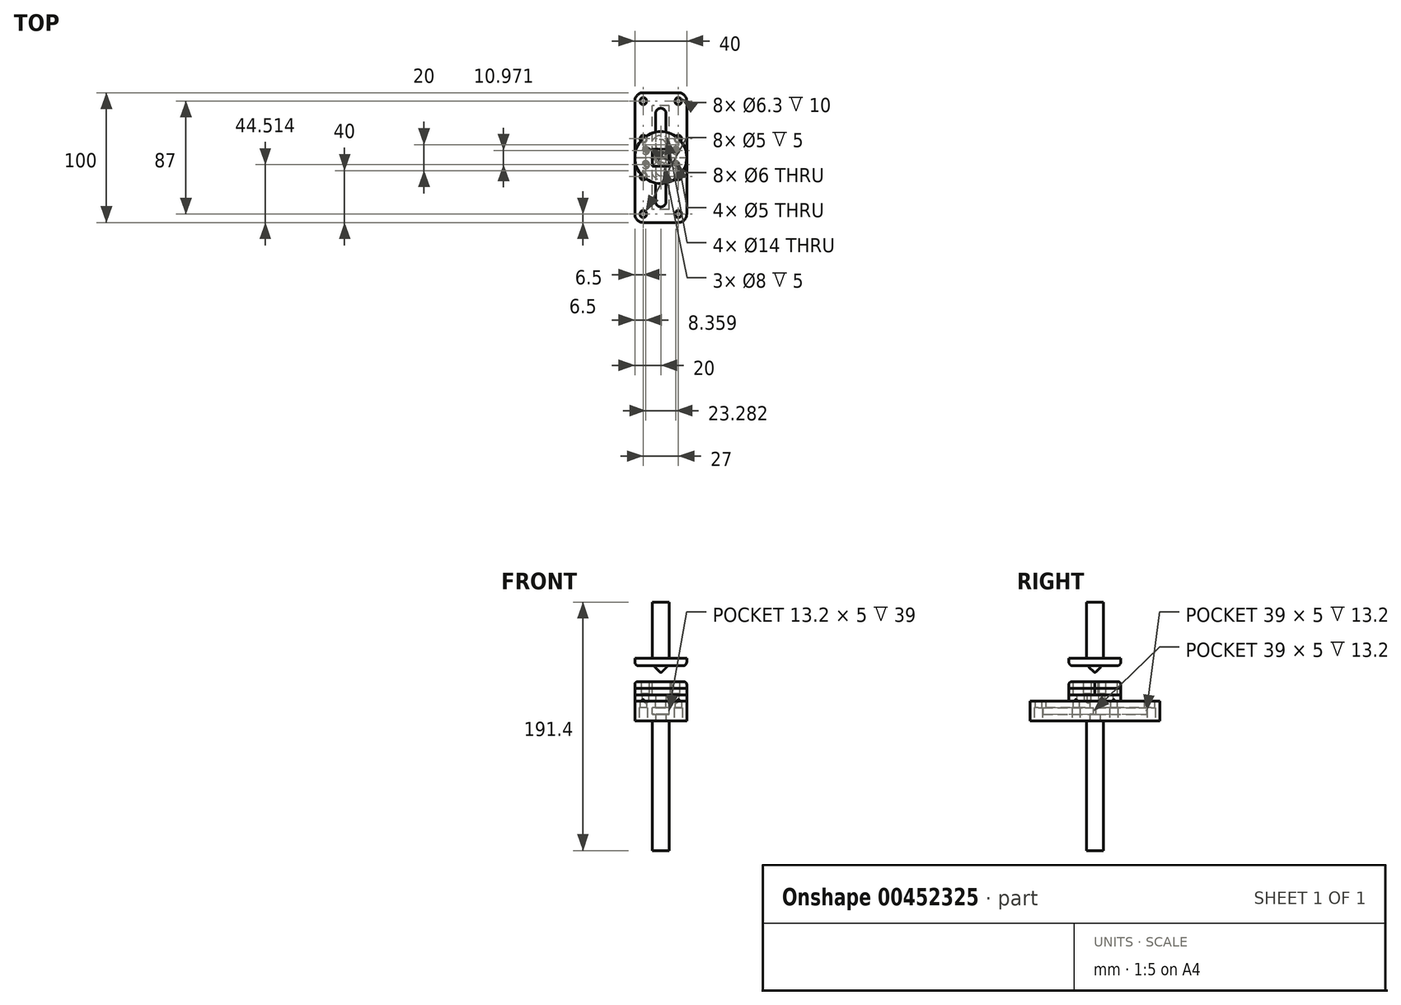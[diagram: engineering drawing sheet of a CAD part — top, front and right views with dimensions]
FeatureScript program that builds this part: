
annotation { "Feature Type Name" : "Feature", "Feature Type Description" : "" }
export const myFeature = defineFeature(function(context is Context, id is Id, definition is map)
    precondition{}
    {
        {
            var Q0;
            Q0=qCreatedBy(makeId("Top.planeOp"),FACE);
            var sketch = newSketch(context, id + "F0", { "sketchPlane" : qUnion([Q0])});
            skLineSegment(sketch, "E0.bottom", {"start": v(6.5, 6.5) * mm, "end": v(-6.5, 6.5) * mm});
            skLineSegment(sketch, "E0.top", {"start": v(6.5, -6.5) * mm, "end": v(-6.5, -6.5) * mm});
            skLineSegment(sketch, "E0.left", {"start": v(6.5, 6.5) * mm, "end": v(6.5, -6.5) * mm});
            skLineSegment(sketch, "E0.right", {"start": v(-6.5, 6.5) * mm, "end": v(-6.5, -6.5) * mm});
            skPoint(sketch, "E0.middle", {"position": v(0, 0) * mm});
            skSolve(sketch);
        }
        {
            var Q0;
            Q0 = qSketchRegion(id + "F0", true);
            extrude(context, id + "F1", {"entities" : qUnion([Q0]), "oppositeDirection" : true, "depth" : 100 * mm});
        }
        {
            var Q0;
            Q0=qCreatedBy(makeId("Top.planeOp"),FACE);
            var sketch = newSketch(context, id + "F2", { "sketchPlane" : qUnion([Q0])});
            skLineSegment(sketch, "E1.bottom", {"start": v(20, 50) * mm, "end": v(-20, 50) * mm});
            skLineSegment(sketch, "E1.top", {"start": v(20, -50) * mm, "end": v(-20, -50) * mm});
            skLineSegment(sketch, "E1.left", {"start": v(20, 50) * mm, "end": v(20, -50) * mm});
            skLineSegment(sketch, "E1.right", {"start": v(-20, 50) * mm, "end": v(-20, -50) * mm});
            skPoint(sketch, "E1.middle", {"position": v(0, 0) * mm});
            skCircle(sketch, "E2", {"center": v(0, 0) * mm, "radius": 4 * mm});
            skSolve(sketch);
        }
        {
            var Q0;
            Q0 = qSketchRegion(id + "F2", true);
            extrude(context, id + "F3", {"entities" : qUnion([Q0]), "depth" : 5 * mm});
        }
        {
            var Q0;
            Q0=makeQuery(id+"F3.opExtrude","CAP_FACE",FACE,{"disambiguationData":[OSD([sQuery(id+"F2.wireOp",EDGE,"E1.bottom"),sQuery(id+"F2.wireOp",EDGE,"E1.top"),sQuery(id+"F2.wireOp",EDGE,"E1.left"),sQuery(id+"F2.wireOp",EDGE,"E1.right")])],"isStart":false});
            var sketch = newSketch(context, id + "F4", { "sketchPlane" : qUnion([Q0])});
            skLineSegment(sketch, "E3.bottom", {"start": v(-20, -50) * mm, "end": v(20, -50) * mm});
            skLineSegment(sketch, "E3.top", {"start": v(-20, 50) * mm, "end": v(20, 50) * mm});
            skLineSegment(sketch, "E3.left", {"start": v(-20, -50) * mm, "end": v(-20, 50) * mm});
            skLineSegment(sketch, "E3.right", {"start": v(20, -50) * mm, "end": v(20, 50) * mm});
            skLineSegment(sketch, "E4.bottom", {"start": v(6.6, -40) * mm, "end": v(-6.6, -40) * mm});
            skLineSegment(sketch, "E4.top", {"start": v(6.6, 40) * mm, "end": v(-6.6, 40) * mm});
            skLineSegment(sketch, "E4.left", {"start": v(6.6, -40) * mm, "end": v(6.6, 40) * mm});
            skLineSegment(sketch, "E4.right", {"start": v(-6.6, -40) * mm, "end": v(-6.6, 40) * mm});
            skPoint(sketch, "E4.middle", {"position": v(0, 0) * mm});
            skSolve(sketch);
        }
        {
            var Q0;
            Q0 = qSketchRegion(id + "F4", true);
            extrude(context, id + "F5", {"entities" : qUnion([Q0]), "depth" : 5 * mm});
        }
        {
            var Q0;
            Q0=makeQuery(id+"F5.opExtrude","CAP_FACE",FACE,{"disambiguationData":[OSD([sQuery(id+"F4.wireOp",EDGE,"E3.bottom"),sQuery(id+"F4.wireOp",EDGE,"E3.top"),sQuery(id+"F4.wireOp",EDGE,"E3.left"),sQuery(id+"F4.wireOp",EDGE,"E3.right"),sQuery(id+"F4.wireOp",EDGE,"E4.bottom"),sQuery(id+"F4.wireOp",EDGE,"E4.top"),sQuery(id+"F4.wireOp",EDGE,"E4.left"),sQuery(id+"F4.wireOp",EDGE,"E4.right")])],"isStart":false});
            var sketch = newSketch(context, id + "F6", { "sketchPlane" : qUnion([Q0])});
            skLineSegment(sketch, "E5.bottom", {"start": v(-20, -50) * mm, "end": v(20, -50) * mm});
            skLineSegment(sketch, "E5.top", {"start": v(-20, 50) * mm, "end": v(20, 50) * mm});
            skLineSegment(sketch, "E5.left", {"start": v(-20, -50) * mm, "end": v(-20, 50) * mm});
            skLineSegment(sketch, "E5.right", {"start": v(20, -50) * mm, "end": v(20, 50) * mm});
            skLineSegment(sketch, "E6.bottom", {"start": v(4, 38) * mm, "end": v(-4, 38) * mm});
            skLineSegment(sketch, "E6.top", {"start": v(4, -38) * mm, "end": v(-4, -38) * mm});
            skLineSegment(sketch, "E6.left", {"start": v(4, 38) * mm, "end": v(4, -38) * mm});
            skLineSegment(sketch, "E6.right", {"start": v(-4, 38) * mm, "end": v(-4, -38) * mm});
            skPoint(sketch, "E6.middle", {"position": v(0, 0) * mm});
            skSolve(sketch);
        }
        {
            var Q0;
            Q0 = qSketchRegion(id + "F6", true);
            extrude(context, id + "F7", {"entities" : qUnion([Q0]), "depth" : 5 * mm});
        }
        {
            var Q0;
            Q0=makeQuery(id+"F7.opExtrude","CAP_FACE",FACE,{"disambiguationData":[OSD([sQuery(id+"F6.wireOp",EDGE,"E5.bottom"),sQuery(id+"F6.wireOp",EDGE,"E5.top"),sQuery(id+"F6.wireOp",EDGE,"E5.left"),sQuery(id+"F6.wireOp",EDGE,"E5.right"),sQuery(id+"F6.wireOp",EDGE,"E6.bottom"),sQuery(id+"F6.wireOp",EDGE,"E6.top"),sQuery(id+"F6.wireOp",EDGE,"E6.left"),sQuery(id+"F6.wireOp",EDGE,"E6.right")])],"isStart":false});
            var sketch = newSketch(context, id + "F8", { "sketchPlane" : qUnion([Q0])});
            skArc(sketch, "E7", {"start": v(-20, 0) * mm, "mid": v(0, -20) * mm, "end": v(20, 0) * mm});
            skLineSegment(sketch, "E8", {"start": v(-20, 0) * mm, "end": v(20, 0) * mm});
            skCircle(sketch, "E9", {"center": v(0, -10) * mm, "radius": 4 * mm});
            skSolve(sketch);
        }
        {
            var Q0;
            Q0 = qSketchRegion(id + "F8", true);
            extrude(context, id + "F9", {"entities" : qUnion([Q0]), "depth" : 5 * mm});
        }
        {
            var Q0;
            Q0=makeQuery(id+"F9.opExtrude","SWEPT_BODY",BODY,{"disambiguationData":[OSD([sQuery(id+"F8.wireOp",EDGE,"E7"),sQuery(id+"F8.wireOp",EDGE,"E8"),sQuery(id+"F8.wireOp",EDGE,"E9")])]});
            var Q1;
            Q1=qCreatedBy(makeId("Front.planeOp"),FACE);
            mirror(context, id + "F10", {"entities" : qUnion([Q0]), "mirrorPlane" : qUnion([Q1])});
        }
        {
            var Q0;
            Q0=makeQuery(id+"F9.opExtrude","CAP_FACE",FACE,{"disambiguationData":[OSD([sQuery(id+"F8.wireOp",EDGE,"E7"),sQuery(id+"F8.wireOp",EDGE,"E8"),sQuery(id+"F8.wireOp",EDGE,"E9")])],"isStart":false});
            var sketch = newSketch(context, id + "F11", { "sketchPlane" : qUnion([Q0])});
            skArc(sketch, "E10", {"start": v(-20, 0) * mm, "mid": v(0, -20) * mm, "end": v(20, 0) * mm});
            skLineSegment(sketch, "E11", {"start": v(-20, 0) * mm, "end": v(20, 0) * mm});
            skCircle(sketch, "E12", {"center": v(0, -10) * mm, "radius": 7 * mm});
            skSolve(sketch);
        }
        {
            var Q0;
            Q0 = qSketchRegion(id + "F11", true);
            extrude(context, id + "F12", {"entities" : qUnion([Q0]), "depth" : 5 * mm});
        }
        {
            var Q0;
            Q0=makeQuery(id+"F12.opExtrude","SWEPT_BODY",BODY,{"disambiguationData":[OSD([sQuery(id+"F11.wireOp",EDGE,"E10"),sQuery(id+"F11.wireOp",EDGE,"E11"),sQuery(id+"F11.wireOp",EDGE,"E12")])]});
            var Q1;
            Q1=qCreatedBy(makeId("Front.planeOp"),FACE);
            mirror(context, id + "F13", {"entities" : qUnion([Q0]), "mirrorPlane" : qUnion([Q1])});
        }
        {
            var Q0;
            Q0=makeQuery(id+"F3.opExtrude","SWEPT_EDGE",EDGE,{"disambiguationData":[OSD([sQuery(id+"F2.wireOp",EDGE,"E1.top"),sQuery(id+"F2.wireOp",EDGE,"E1.left")])]});
            var Q1;
            Q1=makeQuery(id+"F5.opExtrude","SWEPT_EDGE",EDGE,{"disambiguationData":[OSD([sQuery(id+"F4.wireOp",EDGE,"E3.bottom"),sQuery(id+"F4.wireOp",EDGE,"E3.right")])]});
            var Q2;
            Q2=makeQuery(id+"F7.opExtrude","SWEPT_EDGE",EDGE,{"disambiguationData":[OSD([sQuery(id+"F6.wireOp",EDGE,"E5.bottom"),sQuery(id+"F6.wireOp",EDGE,"E5.right")])]});
            var Q3;
            Q3=makeQuery(id+"F3.opExtrude","SWEPT_EDGE",EDGE,{"disambiguationData":[OSD([sQuery(id+"F2.wireOp",EDGE,"E1.top"),sQuery(id+"F2.wireOp",EDGE,"E1.right")])]});
            var Q4;
            Q4=makeQuery(id+"F5.opExtrude","SWEPT_EDGE",EDGE,{"disambiguationData":[OSD([sQuery(id+"F4.wireOp",EDGE,"E3.bottom"),sQuery(id+"F4.wireOp",EDGE,"E3.left")])]});
            var Q5;
            Q5=makeQuery(id+"F7.opExtrude","SWEPT_EDGE",EDGE,{"disambiguationData":[OSD([sQuery(id+"F6.wireOp",EDGE,"E5.bottom"),sQuery(id+"F6.wireOp",EDGE,"E5.left")])]});
            var Q6;
            Q6=makeQuery(id+"F3.opExtrude","SWEPT_EDGE",EDGE,{"disambiguationData":[OSD([sQuery(id+"F2.wireOp",EDGE,"E1.bottom"),sQuery(id+"F2.wireOp",EDGE,"E1.right")])]});
            var Q7;
            Q7=makeQuery(id+"F5.opExtrude","SWEPT_EDGE",EDGE,{"disambiguationData":[OSD([sQuery(id+"F4.wireOp",EDGE,"E3.top"),sQuery(id+"F4.wireOp",EDGE,"E3.left")])]});
            var Q8;
            Q8=makeQuery(id+"F7.opExtrude","SWEPT_EDGE",EDGE,{"disambiguationData":[OSD([sQuery(id+"F6.wireOp",EDGE,"E5.top"),sQuery(id+"F6.wireOp",EDGE,"E5.left")])]});
            var Q9;
            Q9=makeQuery(id+"F7.opExtrude","SWEPT_EDGE",EDGE,{"disambiguationData":[OSD([sQuery(id+"F6.wireOp",EDGE,"E5.top"),sQuery(id+"F6.wireOp",EDGE,"E5.right")])]});
            var Q10;
            Q10=makeQuery(id+"F5.opExtrude","SWEPT_EDGE",EDGE,{"disambiguationData":[OSD([sQuery(id+"F4.wireOp",EDGE,"E3.top"),sQuery(id+"F4.wireOp",EDGE,"E3.right")])]});
            var Q11;
            Q11=makeQuery(id+"F3.opExtrude","SWEPT_EDGE",EDGE,{"disambiguationData":[OSD([sQuery(id+"F2.wireOp",EDGE,"E1.bottom"),sQuery(id+"F2.wireOp",EDGE,"E1.left")])]});
            fillet(context, id + "F14", {"entities" : qUnion([Q0, Q1, Q2, Q3, Q4, Q5, Q6, Q7, Q8, Q9, Q10, Q11]), "radius" : 6.5 * mm, "tangentPropagation" : true, "allowEdgeOverflow" : false});
        }
        {
            var Q0;
            Q0=makeQuery(id+"F7.opExtrude","SWEPT_EDGE",EDGE,{"disambiguationData":[OSD([sQuery(id+"F6.wireOp",EDGE,"E6.bottom"),sQuery(id+"F6.wireOp",EDGE,"E6.left")])]});
            var Q1;
            Q1=makeQuery(id+"F7.opExtrude","SWEPT_EDGE",EDGE,{"disambiguationData":[OSD([sQuery(id+"F6.wireOp",EDGE,"E6.bottom"),sQuery(id+"F6.wireOp",EDGE,"E6.right")])]});
            var Q2;
            Q2=makeQuery(id+"F7.opExtrude","SWEPT_EDGE",EDGE,{"disambiguationData":[OSD([sQuery(id+"F6.wireOp",EDGE,"E6.top"),sQuery(id+"F6.wireOp",EDGE,"E6.right")])]});
            var Q3;
            Q3=makeQuery(id+"F7.opExtrude","SWEPT_EDGE",EDGE,{"disambiguationData":[OSD([sQuery(id+"F6.wireOp",EDGE,"E6.top"),sQuery(id+"F6.wireOp",EDGE,"E6.left")])]});
            fillet(context, id + "F15", {"entities" : qUnion([Q0, Q1, Q2, Q3]), "radius" : 4 * mm, "tangentPropagation" : true, "allowEdgeOverflow" : false});
        }
        {
            var Q0;
            Q0=makeQuery(id+"F3.opExtrude","CAP_FACE",FACE,{"disambiguationData":[OSD([sQuery(id+"F2.wireOp",EDGE,"E1.bottom"),sQuery(id+"F2.wireOp",EDGE,"E1.top"),sQuery(id+"F2.wireOp",EDGE,"E1.left"),sQuery(id+"F2.wireOp",EDGE,"E1.right")])],"isStart":true});
            var sketch = newSketch(context, id + "F16", { "sketchPlane" : qUnion([Q0])});
            skCircle(sketch, "E13", {"center": v(13.5, 43.5) * mm, "radius": 3 * mm});
            skCircle(sketch, "E14.0.1.0", {"center": v(13.5, 14.5) * mm, "radius": 3 * mm});
            skCircle(sketch, "E14.0.2.0", {"center": v(13.5, -14.5) * mm, "radius": 3 * mm});
            skCircle(sketch, "E14.0.3.0", {"center": v(13.5, -43.5) * mm, "radius": 3 * mm});
            skCircle(sketch, "E14.1.0.0", {"center": v(-13.5, 43.5) * mm, "radius": 3 * mm});
            skCircle(sketch, "E14.1.1.0", {"center": v(-13.5, 14.5) * mm, "radius": 3 * mm});
            skCircle(sketch, "E14.1.2.0", {"center": v(-13.5, -14.5) * mm, "radius": 3 * mm});
            skCircle(sketch, "E14.1.3.0", {"center": v(-13.5, -43.5) * mm, "radius": 3 * mm});
            skLineSegment(sketch, "E14.direction1", {"start": v(13.5, 43.5) * mm, "end": v(-13.5, 43.5) * mm, "construction": true});
            skLineSegment(sketch, "E14.direction2", {"start": v(13.5, 43.5) * mm, "end": v(13.5, 14.5) * mm, "construction": true});
            skSolve(sketch);
        }
        {
            var Q0;
            Q0=sQuery(id+"F16.wireOp",VERTEX,"E14.direction1.end");
            var Q1;
            Q1=sQuery(id+"F16.wireOp",VERTEX,"E14.1.1.0.center");
            var Q2;
            Q2=sQuery(id+"F16.wireOp",VERTEX,"E14.0.1.0.center");
            var Q3;
            Q3=sQuery(id+"F16.wireOp",VERTEX,"E13.center");
            var Q4;
            Q4=sQuery(id+"F16.wireOp",VERTEX,"E14.0.2.0.center");
            var Q5;
            Q5=sQuery(id+"F16.wireOp",VERTEX,"E14.1.2.0.center");
            var Q6;
            Q6=sQuery(id+"F16.wireOp",VERTEX,"E14.1.3.0.center");
            var Q7;
            Q7=sQuery(id+"F16.wireOp",VERTEX,"E14.0.3.0.center");
            var Q8;
            Q8=makeQuery(id+"F9.opExtrude","SWEPT_BODY",BODY,{"disambiguationData":[OSD([sQuery(id+"F8.wireOp",EDGE,"E7"),sQuery(id+"F8.wireOp",EDGE,"E8"),sQuery(id+"F8.wireOp",EDGE,"E9")])]});
            var Q9;
            Q9=makeQuery(id+"F12.opExtrude","SWEPT_BODY",BODY,{"disambiguationData":[OSD([sQuery(id+"F11.wireOp",EDGE,"E10"),sQuery(id+"F11.wireOp",EDGE,"E11"),sQuery(id+"F11.wireOp",EDGE,"E12")])]});
            var Q10;
            Q10=makeQuery(id+"F3.opExtrude","SWEPT_BODY",BODY,{"disambiguationData":[OSD([sQuery(id+"F2.wireOp",EDGE,"E1.bottom"),sQuery(id+"F2.wireOp",EDGE,"E1.top"),sQuery(id+"F2.wireOp",EDGE,"E1.left"),sQuery(id+"F2.wireOp",EDGE,"E1.right")])]});
            var Q11;
            Q11=makeQuery(id+"F5.opExtrude","SWEPT_BODY",BODY,{"disambiguationData":[OSD([sQuery(id+"F4.wireOp",EDGE,"E3.bottom"),sQuery(id+"F4.wireOp",EDGE,"E3.top"),sQuery(id+"F4.wireOp",EDGE,"E3.left"),sQuery(id+"F4.wireOp",EDGE,"E3.right"),sQuery(id+"F4.wireOp",EDGE,"E4.bottom"),sQuery(id+"F4.wireOp",EDGE,"E4.top"),sQuery(id+"F4.wireOp",EDGE,"E4.left"),sQuery(id+"F4.wireOp",EDGE,"E4.right")])]});
            var Q12;
            Q12=makeQuery(id+"F7.opExtrude","SWEPT_BODY",BODY,{"disambiguationData":[OSD([sQuery(id+"F6.wireOp",EDGE,"E5.bottom"),sQuery(id+"F6.wireOp",EDGE,"E5.top"),sQuery(id+"F6.wireOp",EDGE,"E5.left"),sQuery(id+"F6.wireOp",EDGE,"E5.right"),sQuery(id+"F6.wireOp",EDGE,"E6.bottom"),sQuery(id+"F6.wireOp",EDGE,"E6.top"),sQuery(id+"F6.wireOp",EDGE,"E6.left"),sQuery(id+"F6.wireOp",EDGE,"E6.right")])]});
            var Q13;
            Q13=makeQuery(id+"F10.opPattern","COPY",BODY,{"derivedFrom":makeQuery(id+"F9.opExtrude","SWEPT_BODY",BODY,{"disambiguationData":[OSD([sQuery(id+"F8.wireOp",EDGE,"E7"),sQuery(id+"F8.wireOp",EDGE,"E8"),sQuery(id+"F8.wireOp",EDGE,"E9")])]}),"instanceName":"1"});
            var Q14;
            Q14=makeQuery(id+"F13.opPattern","COPY",BODY,{"derivedFrom":makeQuery(id+"F12.opExtrude","SWEPT_BODY",BODY,{"disambiguationData":[OSD([sQuery(id+"F11.wireOp",EDGE,"E10"),sQuery(id+"F11.wireOp",EDGE,"E11"),sQuery(id+"F11.wireOp",EDGE,"E12")])]}),"instanceName":"1"});
            hole(context, id + "F17", {"style" : HoleStyle.SIMPLE, "endStyle" : HoleEndStyle.BLIND_IN_LAST, "standardTappedOrClearance" : lookupTablePath({ "fit" : "Close", "standard" : "ISO", "engagement" : "75%", "pitch" : "1 mm", "size" : "M6", "type" : "Clearance & tapped" }), "standardBlindInLast" : lookupTablePath({ "standard" : "ISO", "fit" : "Close", "engagement" : "75%", "pitch" : "1 mm", "size" : "M6", "type" : "Clearance & tapped" }), "holeDiameter" : 6.3 * mm, "tapDrillDiameter" : 5 * mm, "showTappedDepth" : true, "holeDepth" : 5 * mm, "isTappedThrough" : true, "tappedDepth" : 5 * mm, "tapClearance" : 0, "locations" : qUnion([Q0, Q1, Q2, Q3, Q4, Q5, Q6, Q7]), "scope" : qUnion([Q8, Q9, Q10, Q11, Q12, Q13, Q14]), "majorDiameter" : 6 * mm});
        }
        {
            var Q0;
            Q0=makeQuery(id+"F12.opExtrude","CAP_FACE",FACE,{"disambiguationData":[OSD([sQuery(id+"F11.wireOp",EDGE,"E10"),sQuery(id+"F11.wireOp",EDGE,"E11"),sQuery(id+"F11.wireOp",EDGE,"E12")])],"isStart":false});
            var sketch = newSketch(context, id + "F18", { "sketchPlane" : qUnion([Q0])});
            skArc(sketch, "E15", {"start": v(-20, 0) * mm, "mid": v(0, -20) * mm, "end": v(20, 0) * mm});
            skLineSegment(sketch, "E16", {"start": v(-20, 0) * mm, "end": v(20, 0) * mm});
            skCircle(sketch, "E17", {"center": v(0, -10) * mm, "radius": 7 * mm});
            skSolve(sketch);
        }
        {
            var Q0;
            Q0 = qSketchRegion(id + "F18", true);
            extrude(context, id + "F19", {"entities" : qUnion([Q0]), "depth" : 5 * mm});
        }
        {
            var Q0;
            Q0=makeQuery(id+"F19.opExtrude","SWEPT_BODY",BODY,{"disambiguationData":[OSD([sQuery(id+"F18.wireOp",EDGE,"E15"),sQuery(id+"F18.wireOp",EDGE,"E16"),sQuery(id+"F18.wireOp",EDGE,"E17")])]});
            var Q1;
            Q1=qCreatedBy(makeId("Front.planeOp"),FACE);
            mirror(context, id + "F20", {"entities" : qUnion([Q0]), "mirrorPlane" : qUnion([Q1])});
        }
        {
            var Q0;
            Q0=makeQuery(id+"F19.opExtrude","CAP_FACE",FACE,{"disambiguationData":[OSD([sQuery(id+"F18.wireOp",EDGE,"E15"),sQuery(id+"F18.wireOp",EDGE,"E16"),sQuery(id+"F18.wireOp",EDGE,"E17")])],"isStart":false});
            var sketch = newSketch(context, id + "F21", { "sketchPlane" : qUnion([Q0])});
            skCircle(sketch, "E18", {"center": v(11.64, -5.49) * mm, "radius": 2.99 * mm});
            skCircle(sketch, "E19.MirrorC", {"center": v(-11.64, -5.49) * mm, "radius": 2.99 * mm});
            skCircle(sketch, "E20.MirrorC", {"center": v(11.64, 5.49) * mm, "radius": 2.99 * mm});
            skCircle(sketch, "E21.MirrorC", {"center": v(-11.64, 5.49) * mm, "radius": 2.99 * mm});
            skSolve(sketch);
        }
        {
            var Q0;
            Q0=sQuery(id+"F21.wireOp",VERTEX,"E18.center");
            var Q1;
            Q1=sQuery(id+"F21.wireOp",VERTEX,"E19.MirrorC.center");
            var Q2;
            Q2=sQuery(id+"F21.wireOp",VERTEX,"E20.MirrorC.center");
            var Q3;
            Q3=sQuery(id+"F21.wireOp",VERTEX,"E21.MirrorC.center");
            var Q4;
            Q4=makeQuery(id+"F9.opExtrude","SWEPT_BODY",BODY,{"disambiguationData":[OSD([sQuery(id+"F8.wireOp",EDGE,"E7"),sQuery(id+"F8.wireOp",EDGE,"E8"),sQuery(id+"F8.wireOp",EDGE,"E9")])]});
            var Q5;
            Q5=makeQuery(id+"F12.opExtrude","SWEPT_BODY",BODY,{"disambiguationData":[OSD([sQuery(id+"F11.wireOp",EDGE,"E10"),sQuery(id+"F11.wireOp",EDGE,"E11"),sQuery(id+"F11.wireOp",EDGE,"E12")])]});
            var Q6;
            Q6=makeQuery(id+"F10.opPattern","COPY",BODY,{"derivedFrom":makeQuery(id+"F9.opExtrude","SWEPT_BODY",BODY,{"disambiguationData":[OSD([sQuery(id+"F8.wireOp",EDGE,"E7"),sQuery(id+"F8.wireOp",EDGE,"E8"),sQuery(id+"F8.wireOp",EDGE,"E9")])]}),"instanceName":"1"});
            var Q7;
            Q7=makeQuery(id+"F13.opPattern","COPY",BODY,{"derivedFrom":makeQuery(id+"F12.opExtrude","SWEPT_BODY",BODY,{"disambiguationData":[OSD([sQuery(id+"F11.wireOp",EDGE,"E10"),sQuery(id+"F11.wireOp",EDGE,"E11"),sQuery(id+"F11.wireOp",EDGE,"E12")])]}),"instanceName":"1"});
            var Q8;
            Q8=makeQuery(id+"F19.opExtrude","SWEPT_BODY",BODY,{"disambiguationData":[OSD([sQuery(id+"F18.wireOp",EDGE,"E15"),sQuery(id+"F18.wireOp",EDGE,"E16"),sQuery(id+"F18.wireOp",EDGE,"E17")])]});
            var Q9;
            Q9=makeQuery(id+"F20.opPattern","COPY",BODY,{"derivedFrom":makeQuery(id+"F19.opExtrude","SWEPT_BODY",BODY,{"disambiguationData":[OSD([sQuery(id+"F18.wireOp",EDGE,"E15"),sQuery(id+"F18.wireOp",EDGE,"E16"),sQuery(id+"F18.wireOp",EDGE,"E17")])]}),"instanceName":"1"});
            hole(context, id + "F22", {"style" : HoleStyle.SIMPLE, "endStyle" : HoleEndStyle.BLIND, "holeDiameter" : 6 * mm, "holeDepth" : 9 * mm, "isTappedThrough" : true, "tappedDepth" : 5 * mm, "tapClearance" : 0, "locations" : qUnion([Q0, Q1, Q2, Q3]), "scope" : qUnion([Q4, Q5, Q6, Q7, Q8, Q9])});
        }
        {
            var Q0;
            Q0=sQuery(id+"F21.wireOp",VERTEX,"E19.MirrorC.center");
            var Q1;
            Q1=sQuery(id+"F21.wireOp",VERTEX,"E20.MirrorC.center");
            var Q2;
            Q2=sQuery(id+"F21.wireOp",VERTEX,"E21.MirrorC.center");
            var Q3;
            Q3=sQuery(id+"F21.wireOp",VERTEX,"E20.MirrorC.center");
            var Q4;
            Q4=sQuery(id+"F21.wireOp",VERTEX,"E18.center");
            var Q5;
            Q5=makeQuery(id+"F9.opExtrude","SWEPT_BODY",BODY,{"disambiguationData":[OSD([sQuery(id+"F8.wireOp",EDGE,"E7"),sQuery(id+"F8.wireOp",EDGE,"E8"),sQuery(id+"F8.wireOp",EDGE,"E9")])]});
            var Q6;
            Q6=makeQuery(id+"F7.opExtrude","SWEPT_BODY",BODY,{"disambiguationData":[OSD([sQuery(id+"F6.wireOp",EDGE,"E5.bottom"),sQuery(id+"F6.wireOp",EDGE,"E5.top"),sQuery(id+"F6.wireOp",EDGE,"E5.left"),sQuery(id+"F6.wireOp",EDGE,"E5.right"),sQuery(id+"F6.wireOp",EDGE,"E6.bottom"),sQuery(id+"F6.wireOp",EDGE,"E6.top"),sQuery(id+"F6.wireOp",EDGE,"E6.left"),sQuery(id+"F6.wireOp",EDGE,"E6.right")])]});
            var Q7;
            Q7=makeQuery(id+"F10.opPattern","COPY",BODY,{"derivedFrom":makeQuery(id+"F9.opExtrude","SWEPT_BODY",BODY,{"disambiguationData":[OSD([sQuery(id+"F8.wireOp",EDGE,"E7"),sQuery(id+"F8.wireOp",EDGE,"E8"),sQuery(id+"F8.wireOp",EDGE,"E9")])]}),"instanceName":"1"});
            hole(context, id + "F23", {"style" : HoleStyle.SIMPLE, "endStyle" : HoleEndStyle.BLIND, "holeDiameter" : 5 * mm, "holeDepth" : 5 * mm, "isTappedThrough" : true, "tappedDepth" : 5 * mm, "tapClearance" : 0, "locations" : qUnion([Q0, Q1, Q2, Q3, Q4]), "scope" : qUnion([Q5, Q6, Q7])});
        }
        {
            var Q0;
            Q0=makeQuery(id+"F20.opPattern","COPY",EDGE,{"derivedFrom":makeQuery(id+"F19.opExtrude","CAP_EDGE",EDGE,{"disambiguationData":[OSD([sQuery(id+"F18.wireOp",EDGE,"E15")])],"isStart":false}),"instanceName":"1"});
            var Q1;
            Q1=makeQuery(id+"F19.opExtrude","CAP_EDGE",EDGE,{"disambiguationData":[OSD([sQuery(id+"F18.wireOp",EDGE,"E15")])],"isStart":false});
            fillet(context, id + "F24", {"entities" : qUnion([Q0, Q1]), "radius" : 2 * mm, "tangentPropagation" : true, "allowEdgeOverflow" : false});
        }
        {
            var Q0;
            Q0=makeQuery(id+"F21.imprint","IMPRINT",FACE,{"disambiguationData":[TD([[makeQuery(id+"F21.imprint","IMPRINT",EDGE,{"derivedFrom":sQuery(id+"F21.wireOp",EDGE,"E18")}),-1.0]])]});
            var sketch = newSketch(context, id + "F25", { "sketchPlane" : qUnion([Q0])});
            skLineSegment(sketch, "E22.bottom", {"start": v(-6.5, -6.5) * mm, "end": v(6.5, -6.5) * mm});
            skLineSegment(sketch, "E22.top", {"start": v(-6.5, 6.5) * mm, "end": v(6.5, 6.5) * mm});
            skLineSegment(sketch, "E22.left", {"start": v(-6.5, -6.5) * mm, "end": v(-6.5, 6.5) * mm});
            skLineSegment(sketch, "E22.right", {"start": v(6.5, -6.5) * mm, "end": v(6.5, 6.5) * mm});
            skPoint(sketch, "E22.middle", {"position": v(0, 0) * mm});
            skSolve(sketch);
        }
        {
            var Q0;
            Q0 = qSketchRegion(id + "F25", true);
            extrude(context, id + "F26", {"entities" : qUnion([Q0]), "depth" : 61.4 * mm, "hasSecondDirection" : true, "secondDirectionOppositeDirection" : false, "secondDirectionDepth" : 18.3 * mm});
        }
        {
            var Q0;
            Q0=makeQuery(id+"F26.opExtrude","CAP_FACE",FACE,{"disambiguationData":[OSD([sQuery(id+"F25.wireOp",EDGE,"E22.bottom"),sQuery(id+"F25.wireOp",EDGE,"E22.top"),sQuery(id+"F25.wireOp",EDGE,"E22.left"),sQuery(id+"F25.wireOp",EDGE,"E22.right")])],"isStart":true});
            var sketch = newSketch(context, id + "F27", { "sketchPlane" : qUnion([Q0])});
            skCircle(sketch, "E23", {"center": v(0, 0) * mm, "radius": 20 * mm});
            skSolve(sketch);
        }
        {
            var Q0;
            Q0 = qSketchRegion(id + "F27", true);
            extrude(context, id + "F28", {"entities" : qUnion([Q0]), "operationType" : NewBodyOperationType.ADD, "depth" : 6 * mm});
        }
        {
            var Q0;
            Q0=makeQuery(id+"F28.opExtrude","CAP_EDGE",EDGE,{"disambiguationData":[OSD([sQuery(id+"F27.wireOp",EDGE,"E23")])],"isStart":false});
            fillet(context, id + "F29", {"entities" : qUnion([Q0]), "radius" : 3 * mm, "tangentPropagation" : true, "allowEdgeOverflow" : false});
        }
        {
            var Q0;
            Q0=makeQuery(id+"F28.opExtrude","CAP_FACE",FACE,{"disambiguationData":[OSD([sQuery(id+"F27.wireOp",EDGE,"E23")])],"isStart":false});
            var sketch = newSketch(context, id + "F30", { "sketchPlane" : qUnion([Q0])});
            skCircle(sketch, "E24", {"center": v(0, 0) * mm, "radius": 5 * mm});
            skSolve(sketch);
        }
        {
            var Q0;
            Q0 = qSketchRegion(id + "F30", true);
            extrude(context, id + "F31", {"entities" : qUnion([Q0]), "depth" : 5 * mm});
        }
        {
            var Q0;
            Q0=makeQuery(id+"F31.opExtrude","CAP_EDGE",EDGE,{"disambiguationData":[OSD([sQuery(id+"F30.wireOp",EDGE,"E24")])],"isStart":false});
            chamfer(context, id + "F32", {"entities" : qUnion([Q0]), "width" : 4.5 * mm, "tangentPropagation" : true});
        }
        {
            var Q0;
            {var subQ0=sQuery(id+"F30.wireOp",EDGE,"E24");Q0=makeQuery(id+"F32.opChamfer","BLEND_EDGE",EDGE,{"blendedFrom":[makeQuery(id+"F31.opExtrude","CAP_EDGE",EDGE,{"disambiguationData":[OSD([subQ0])],"isStart":false}),makeQuery(id+"F31.opExtrude","CAP_FACE",FACE,{"disambiguationData":[OSD([subQ0])],"isStart":false})],"blendedInto":[makeQuery(id+"F31.opExtrude","CAP_FACE",FACE,{"disambiguationData":[OSD([subQ0])],"isStart":false})]});}
            fillet(context, id + "F33", {"entities" : qUnion([Q0]), "radius" : 1 * mm, "tangentPropagation" : true, "allowEdgeOverflow" : false});
        }
        {
            var Q0;
            {var subQ0=sQuery(id+"F30.wireOp",EDGE,"E24");Q0=makeQuery(id+"F32.opChamfer","BLEND_EDGE",EDGE,{"blendedFrom":[makeQuery(id+"F31.opExtrude","CAP_EDGE",EDGE,{"disambiguationData":[OSD([subQ0])],"isStart":false}),makeQuery(id+"F31.opExtrude","SWEPT_FACE",FACE,{"disambiguationData":[OSD([subQ0])]})],"blendedInto":[makeQuery(id+"F31.opExtrude","SWEPT_FACE",FACE,{"disambiguationData":[OSD([subQ0])]})]});}
            fillet(context, id + "F34", {"entities" : qUnion([Q0]), "radius" : 2 * mm, "tangentPropagation" : true, "allowEdgeOverflow" : false});
        }
        {
            var Q0;
            Q0=makeQuery(id+"F5.opExtrude","CAP_FACE",FACE,{"disambiguationData":[OSD([sQuery(id+"F4.wireOp",EDGE,"E3.bottom"),sQuery(id+"F4.wireOp",EDGE,"E3.top"),sQuery(id+"F4.wireOp",EDGE,"E3.left"),sQuery(id+"F4.wireOp",EDGE,"E3.right"),sQuery(id+"F4.wireOp",EDGE,"E4.bottom"),sQuery(id+"F4.wireOp",EDGE,"E4.top"),sQuery(id+"F4.wireOp",EDGE,"E4.left"),sQuery(id+"F4.wireOp",EDGE,"E4.right")])],"isStart":false});
            var sketch = newSketch(context, id + "F35", { "sketchPlane" : qUnion([Q0])});
            skLineSegment(sketch, "E25.bottom", {"start": v(-6.6, 1) * mm, "end": v(6.6, 1) * mm});
            skLineSegment(sketch, "E25.top", {"start": v(-6.6, -1) * mm, "end": v(6.6, -1) * mm});
            skLineSegment(sketch, "E25.left", {"start": v(-6.6, 1) * mm, "end": v(-6.6, -1) * mm});
            skLineSegment(sketch, "E25.right", {"start": v(6.6, 1) * mm, "end": v(6.6, -1) * mm});
            skPoint(sketch, "E25.middle", {"position": v(0, 0) * mm});
            skSolve(sketch);
        }
        {
            var Q0;
            Q0 = qSketchRegion(id + "F35", true);
            extrude(context, id + "F36", {"entities" : qUnion([Q0]), "operationType" : NewBodyOperationType.ADD, "oppositeDirection" : true, "depth" : 5 * mm, "offsetDistance" : 25 * mm});
        }
        {
            var Q0;
            Q0=makeQuery(id+"F7.opExtrude","CAP_FACE",FACE,{"disambiguationData":[OSD([sQuery(id+"F6.wireOp",EDGE,"E5.bottom"),sQuery(id+"F6.wireOp",EDGE,"E5.top"),sQuery(id+"F6.wireOp",EDGE,"E5.left"),sQuery(id+"F6.wireOp",EDGE,"E5.right"),sQuery(id+"F6.wireOp",EDGE,"E6.bottom"),sQuery(id+"F6.wireOp",EDGE,"E6.top"),sQuery(id+"F6.wireOp",EDGE,"E6.left"),sQuery(id+"F6.wireOp",EDGE,"E6.right")])],"isStart":false});
            var sketch = newSketch(context, id + "F37", { "sketchPlane" : qUnion([Q0])});
            skLineSegment(sketch, "E26.bottom", {"start": v(-4, -3.5) * mm, "end": v(4, -3.5) * mm});
            skLineSegment(sketch, "E26.top", {"start": v(-4, 3.5) * mm, "end": v(4, 3.5) * mm});
            skLineSegment(sketch, "E26.left", {"start": v(-4, -3.5) * mm, "end": v(-4, 3.5) * mm});
            skLineSegment(sketch, "E26.right", {"start": v(4, -3.5) * mm, "end": v(4, 3.5) * mm});
            skPoint(sketch, "E26.middle", {"position": v(0, 0) * mm});
            skSolve(sketch);
        }
        {
            var Q0;
            Q0 = qSketchRegion(id + "F37", true);
            extrude(context, id + "F38", {"entities" : qUnion([Q0]), "operationType" : NewBodyOperationType.ADD, "oppositeDirection" : true, "depth" : 5 * mm, "offsetDistance" : 25 * mm});
        }
        {
            var Q0;
            Q0=makeQuery(id+"F38.opExtrude","SWEPT_EDGE",EDGE,{"disambiguationData":[OSD([sQuery(id+"F6.wireOp",EDGE,"E6.left"),sQuery(id+"F37.wireOp",EDGE,"E26.bottom"),sQuery(id+"F37.wireOp",EDGE,"E26.right")])]});
            var Q1;
            Q1=makeQuery(id+"F38.opExtrude","SWEPT_EDGE",EDGE,{"disambiguationData":[OSD([sQuery(id+"F6.wireOp",EDGE,"E6.right"),sQuery(id+"F37.wireOp",EDGE,"E26.bottom"),sQuery(id+"F37.wireOp",EDGE,"E26.left")])]});
            var Q2;
            Q2=makeQuery(id+"F38.opExtrude","SWEPT_EDGE",EDGE,{"disambiguationData":[OSD([sQuery(id+"F6.wireOp",EDGE,"E6.right"),sQuery(id+"F37.wireOp",EDGE,"E26.top"),sQuery(id+"F37.wireOp",EDGE,"E26.left")])]});
            var Q3;
            Q3=makeQuery(id+"F38.opExtrude","SWEPT_EDGE",EDGE,{"disambiguationData":[OSD([sQuery(id+"F6.wireOp",EDGE,"E6.left"),sQuery(id+"F37.wireOp",EDGE,"E26.top"),sQuery(id+"F37.wireOp",EDGE,"E26.right")])]});
            fillet(context, id + "F39", {"entities" : qUnion([Q0, Q1, Q2, Q3]), "radius" : 4 * mm, "tangentPropagation" : true, "allowEdgeOverflow" : false});
        }
    });
